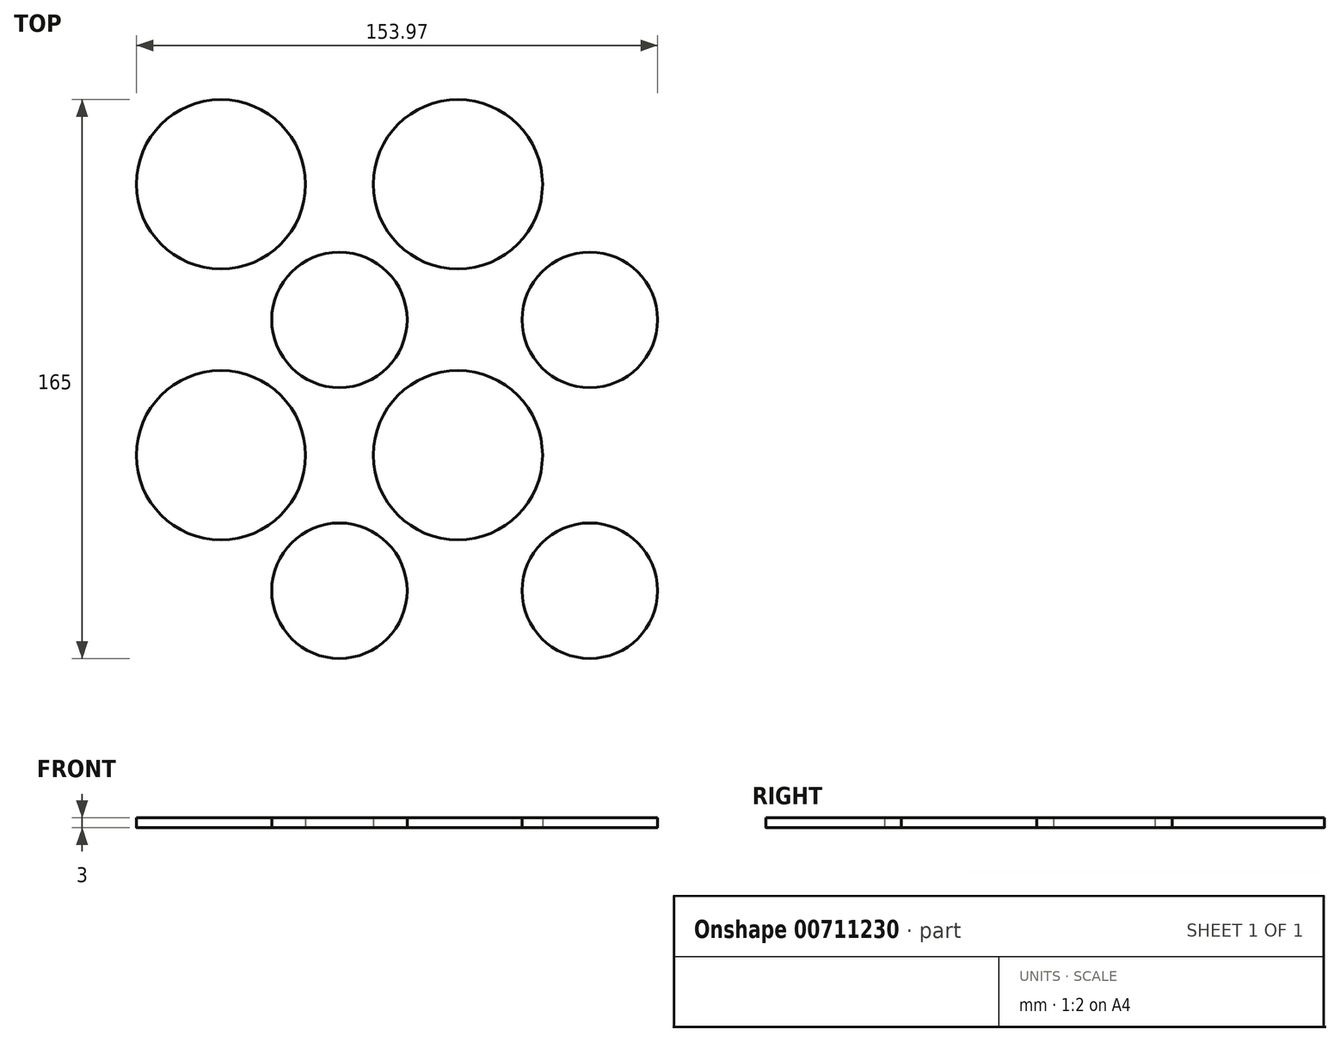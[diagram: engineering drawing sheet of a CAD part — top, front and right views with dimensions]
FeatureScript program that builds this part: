
annotation { "Feature Type Name" : "Feature", "Feature Type Description" : "" }
export const myFeature = defineFeature(function(context is Context, id is Id, definition is map)
    precondition{}
    {
        {
            var Q0;
            Q0=qCreatedBy(makeId("Top.planeOp"),FACE);
            var sketch = newSketch(context, id + "F0", { "sketchPlane" : qUnion([Q0])});
            skCircle(sketch, "E0", {"center": v(-65.35, 80) * mm, "radius": 25 * mm});
            skCircle(sketch, "E1", {"center": v(4.65, 80) * mm, "radius": 25 * mm});
            skCircle(sketch, "E2", {"center": v(-65.35, 0) * mm, "radius": 25 * mm});
            skCircle(sketch, "E3", {"center": v(4.65, 0) * mm, "radius": 25 * mm});
            skCircle(sketch, "E4", {"center": v(-30.35, -40) * mm, "radius": 20 * mm});
            skCircle(sketch, "E5", {"center": v(43.62, -40) * mm, "radius": 20 * mm});
            skCircle(sketch, "E6", {"center": v(-30.35, 40) * mm, "radius": 20 * mm});
            skCircle(sketch, "E7", {"center": v(43.62, 40) * mm, "radius": 20 * mm});
            skSolve(sketch);
        }
        {
            var Q0;
            Q0=makeQuery(id+"F0.imprint","IMPRINT",FACE,{"disambiguationData":[TD([[makeQuery(id+"F0.imprint","IMPRINT",EDGE,{"derivedFrom":sQuery(id+"F0.wireOp",EDGE,"E0")}),1.0]])]});
            var Q1;
            Q1=makeQuery(id+"F0.imprint","IMPRINT",FACE,{"disambiguationData":[TD([[makeQuery(id+"F0.imprint","IMPRINT",EDGE,{"derivedFrom":sQuery(id+"F0.wireOp",EDGE,"E1")}),1.0]])]});
            var Q2;
            Q2=makeQuery(id+"F0.imprint","IMPRINT",FACE,{"disambiguationData":[TD([[makeQuery(id+"F0.imprint","IMPRINT",EDGE,{"derivedFrom":sQuery(id+"F0.wireOp",EDGE,"E7")}),1.0]])]});
            var Q3;
            Q3=makeQuery(id+"F0.imprint","IMPRINT",FACE,{"disambiguationData":[TD([[makeQuery(id+"F0.imprint","IMPRINT",EDGE,{"derivedFrom":sQuery(id+"F0.wireOp",EDGE,"E6")}),1.0]])]});
            var Q4;
            Q4=makeQuery(id+"F0.imprint","IMPRINT",FACE,{"disambiguationData":[TD([[makeQuery(id+"F0.imprint","IMPRINT",EDGE,{"derivedFrom":sQuery(id+"F0.wireOp",EDGE,"E2")}),1.0]])]});
            var Q5;
            Q5=makeQuery(id+"F0.imprint","IMPRINT",FACE,{"disambiguationData":[TD([[makeQuery(id+"F0.imprint","IMPRINT",EDGE,{"derivedFrom":sQuery(id+"F0.wireOp",EDGE,"E3")}),1.0]])]});
            var Q6;
            Q6=makeQuery(id+"F0.imprint","IMPRINT",FACE,{"disambiguationData":[TD([[makeQuery(id+"F0.imprint","IMPRINT",EDGE,{"derivedFrom":sQuery(id+"F0.wireOp",EDGE,"E4")}),1.0]])]});
            var Q7;
            Q7=makeQuery(id+"F0.imprint","IMPRINT",FACE,{"disambiguationData":[TD([[makeQuery(id+"F0.imprint","IMPRINT",EDGE,{"derivedFrom":sQuery(id+"F0.wireOp",EDGE,"E5")}),1.0]])]});
            extrude(context, id + "F1", {"entities" : qUnion([Q0, Q1, Q2, Q3, Q4, Q5, Q6, Q7]), "depth" : 3 * mm, "offsetDistance" : 25 * mm});
        }
        {
            var Q0;
            Q0=makeQuery(id+"F1.opExtrude","CAP_EDGE",EDGE,{"disambiguationData":[OSD([sQuery(id+"F0.wireOp",EDGE,"E0")])],"isStart":true});
            var Q1;
            Q1=makeQuery(id+"F1.opExtrude","CAP_EDGE",EDGE,{"disambiguationData":[OSD([sQuery(id+"F0.wireOp",EDGE,"E2")])],"isStart":true});
            var Q2;
            Q2=makeQuery(id+"F1.opExtrude","CAP_FACE",FACE,{"disambiguationData":[OSD([sQuery(id+"F0.wireOp",EDGE,"E4")])],"isStart":true});
            var Q3;
            Q3=makeQuery(id+"F1.opExtrude","CAP_EDGE",EDGE,{"disambiguationData":[OSD([sQuery(id+"F0.wireOp",EDGE,"E6")])],"isStart":true});
            var Q4;
            Q4=makeQuery(id+"F1.opExtrude","CAP_EDGE",EDGE,{"disambiguationData":[OSD([sQuery(id+"F0.wireOp",EDGE,"E3")])],"isStart":true});
            var Q5;
            Q5=makeQuery(id+"F1.opExtrude","CAP_EDGE",EDGE,{"disambiguationData":[OSD([sQuery(id+"F0.wireOp",EDGE,"E5")])],"isStart":true});
            var Q6;
            Q6=makeQuery(id+"F1.opExtrude","CAP_EDGE",EDGE,{"disambiguationData":[OSD([sQuery(id+"F0.wireOp",EDGE,"E1")])],"isStart":true});
            var Q7;
            Q7=makeQuery(id+"F1.opExtrude","CAP_EDGE",EDGE,{"disambiguationData":[OSD([sQuery(id+"F0.wireOp",EDGE,"E7")])],"isStart":true});
            fillet(context, id + "F2", {"entities" : qUnion([Q0, Q1, Q2, Q3, Q4, Q5, Q6, Q7]), "radius" : 0.2 * mm, "tangentPropagation" : true, "allowEdgeOverflow" : false});
        }
    });
